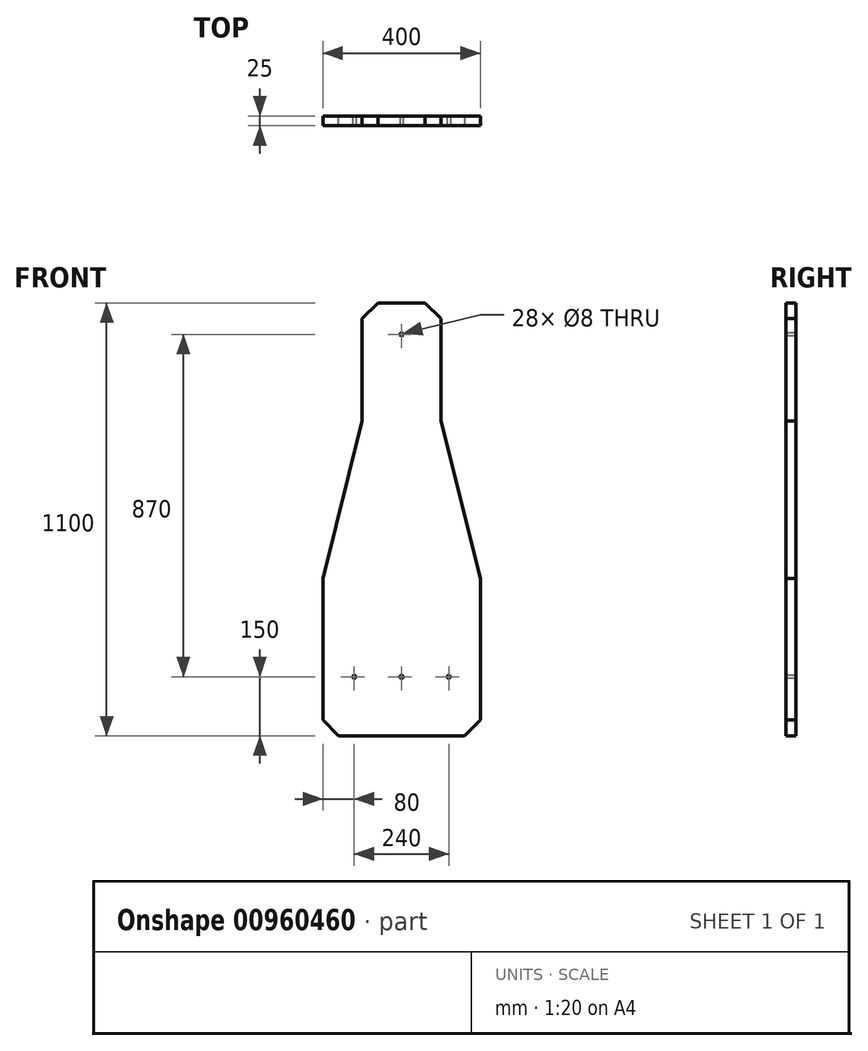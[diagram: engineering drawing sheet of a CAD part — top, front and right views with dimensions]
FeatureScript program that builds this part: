
annotation { "Feature Type Name" : "Feature", "Feature Type Description" : "" }
export const myFeature = defineFeature(function(context is Context, id is Id, definition is map)
    precondition{}
    {
        {
            var Q0;
            Q0=qCreatedBy(makeId("Front.planeOp"),FACE);
            var sketch = newSketch(context, id + "F0", { "sketchPlane" : qUnion([Q0])});
            skLineSegment(sketch, "E0", {"start": v(0, 0) * mm, "end": v(400, 0) * mm});
            skLineSegment(sketch, "E1", {"start": v(400, 0) * mm, "end": v(400, 400) * mm});
            skLineSegment(sketch, "E2", {"start": v(400, 400) * mm, "end": v(300, 800) * mm});
            skLineSegment(sketch, "E3", {"start": v(300, 800) * mm, "end": v(300, 1100) * mm});
            skLineSegment(sketch, "E4", {"start": v(300, 1100) * mm, "end": v(100, 1100) * mm});
            skLineSegment(sketch, "E5", {"start": v(100, 1100) * mm, "end": v(100, 800) * mm});
            skLineSegment(sketch, "E6", {"start": v(0, 0) * mm, "end": v(0, 400) * mm});
            skLineSegment(sketch, "E7", {"start": v(0, 400) * mm, "end": v(100, 800) * mm});
            skSolve(sketch);
        }
        {
            var Q0;
            Q0=makeQuery(id+"F0.imprint","IMPRINT",FACE,{"disambiguationData":[TD([[makeQuery(id+"F0.imprint","IMPRINT",EDGE,{"derivedFrom":sQuery(id+"F0.wireOp",EDGE,"E0")}),1.0]])]});
            extrude(context, id + "F1", {"entities" : qUnion([Q0]), "depth" : 25 * mm, "offsetDistance" : 25 * mm});
        }
        {
            var Q0;
            Q0=makeQuery(id+"F1.opExtrude","CAP_FACE",FACE,{"disambiguationData":[OSD([sQuery(id+"F0.wireOp",EDGE,"E0"),sQuery(id+"F0.wireOp",EDGE,"E1"),sQuery(id+"F0.wireOp",EDGE,"E2"),sQuery(id+"F0.wireOp",EDGE,"E3"),sQuery(id+"F0.wireOp",EDGE,"E4"),sQuery(id+"F0.wireOp",EDGE,"E5"),sQuery(id+"F0.wireOp",EDGE,"E6"),sQuery(id+"F0.wireOp",EDGE,"E7")])],"isStart":false});
            var sketch = newSketch(context, id + "F2", { "sketchPlane" : qUnion([Q0])});
            skCircle(sketch, "E8", {"center": v(200, 1020) * mm, "radius": 4 * mm});
            skCircle(sketch, "E9", {"center": v(80, 150) * mm, "radius": 4 * mm});
            skCircle(sketch, "E10", {"center": v(320, 150) * mm, "radius": 4 * mm});
            skCircle(sketch, "E11", {"center": v(200, 150) * mm, "radius": 4 * mm});
            skSolve(sketch);
        }
        {
            var Q0;
            Q0=makeQuery(id+"F2.imprint","IMPRINT",FACE,{"disambiguationData":[TD([[makeQuery(id+"F2.imprint","IMPRINT",EDGE,{"derivedFrom":sQuery(id+"F2.wireOp",EDGE,"E9")}),1.0]])]});
            var Q1;
            Q1=makeQuery(id+"F2.imprint","IMPRINT",FACE,{"disambiguationData":[TD([[makeQuery(id+"F2.imprint","IMPRINT",EDGE,{"derivedFrom":sQuery(id+"F2.wireOp",EDGE,"E10")}),1.0]])]});
            var Q2;
            Q2=makeQuery(id+"F2.imprint","IMPRINT",FACE,{"disambiguationData":[TD([[makeQuery(id+"F2.imprint","IMPRINT",EDGE,{"derivedFrom":sQuery(id+"F2.wireOp",EDGE,"E8")}),1.0]])]});
            extrude(context, id + "F3", {"entities" : qUnion([Q0, Q1, Q2]), "operationType" : NewBodyOperationType.REMOVE, "endBound" : BoundingType.UP_TO_NEXT, "oppositeDirection" : true, "depth" : 25 * mm, "offsetDistance" : 25 * mm});
        }
        {
            var Q0;
            Q0=makeQuery(id+"F1.opExtrude","SWEPT_EDGE",EDGE,{"disambiguationData":[OSD([sQuery(id+"F0.wireOp",EDGE,"E0"),sQuery(id+"F0.wireOp",EDGE,"E1")])]});
            var Q1;
            Q1=makeQuery(id+"F1.opExtrude","SWEPT_EDGE",EDGE,{"disambiguationData":[OSD([sQuery(id+"F0.wireOp",EDGE,"E0"),sQuery(id+"F0.wireOp",EDGE,"E6")])]});
            var Q2;
            Q2=makeQuery(id+"F1.opExtrude","SWEPT_EDGE",EDGE,{"disambiguationData":[OSD([sQuery(id+"F0.wireOp",EDGE,"E3"),sQuery(id+"F0.wireOp",EDGE,"E4")])]});
            var Q3;
            Q3=makeQuery(id+"F1.opExtrude","SWEPT_EDGE",EDGE,{"disambiguationData":[OSD([sQuery(id+"F0.wireOp",EDGE,"E4"),sQuery(id+"F0.wireOp",EDGE,"E5")])]});
            chamfer(context, id + "F4", {"entities" : qUnion([Q0, Q1, Q2, Q3]), "width" : 40 * mm, "tangentPropagation" : true});
        }
        {
            var Q0;
            Q0=makeQuery(id+"F2.imprint","IMPRINT",FACE,{"disambiguationData":[TD([[makeQuery(id+"F2.imprint","IMPRINT",EDGE,{"derivedFrom":sQuery(id+"F2.wireOp",EDGE,"E11")}),1.0]])]});
            extrude(context, id + "F5", {"entities" : qUnion([Q0]), "operationType" : NewBodyOperationType.REMOVE, "oppositeDirection" : true, "depth" : 25 * mm, "offsetDistance" : 25 * mm});
        }
    });
